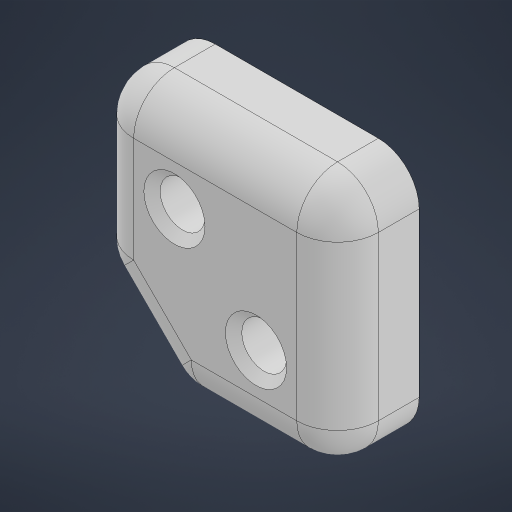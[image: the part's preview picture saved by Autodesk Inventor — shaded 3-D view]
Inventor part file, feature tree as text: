
AUTODESK INVENTOR PART (.ipt)
format: ipt  version: 2024 (Build 280153000, 153)  size: 225,792 bytes
history: native  units: mm
features: extrude x2, fillet x2, sketch x2, other x1, chamfer x1
ambient origin geometry x8: Origin, YZ Plane, XZ Plane, XY Plane, X Axis, Y Axis, Z Axis, Center Point
bodies: Body1 (feature_tree)
feature tree (8):
  other  "솔리드1"
  extrude  "돌출1"  Depth=30.0mm
  fillet  "모깎기1"  Radius=30.0mm
  fillet  "모깎기2"  Radius=20.0mm
  extrude  "돌출2"  Depth=20.0mm
  chamfer  "모따기1"  Distance=10.0mm
  sketch  "스케치1"
  sketch  "스케치2"
